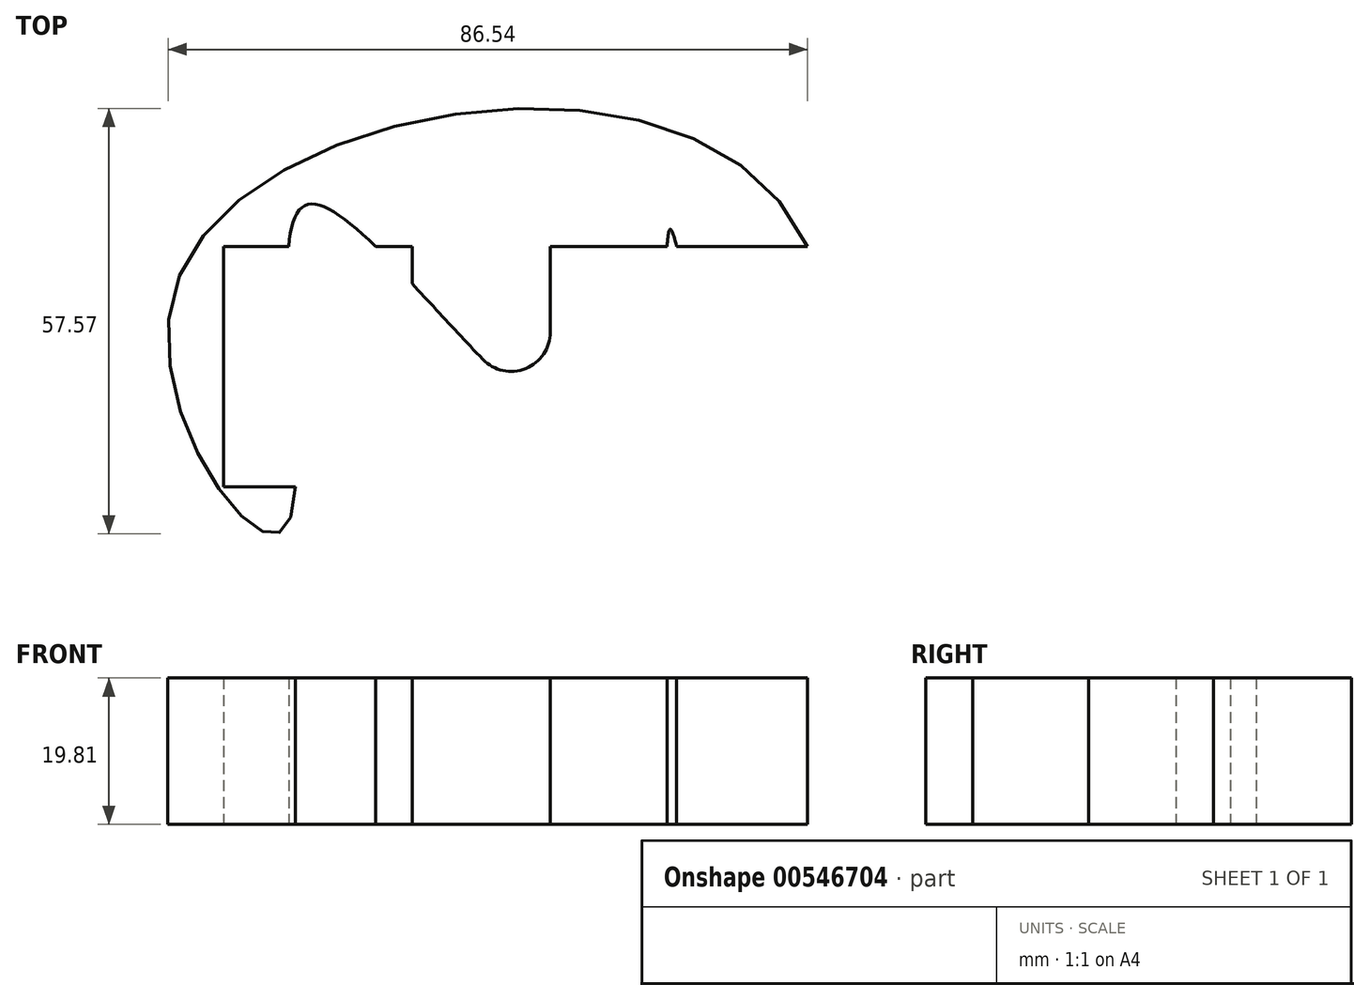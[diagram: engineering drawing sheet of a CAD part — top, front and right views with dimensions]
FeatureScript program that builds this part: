
annotation { "Feature Type Name" : "Feature", "Feature Type Description" : "" }
export const myFeature = defineFeature(function(context is Context, id is Id, definition is map)
    precondition{}
    {
        {
            var Q0;
            Q0=qCreatedBy(makeId("Top.planeOp"),FACE);
            var sketch = newSketch(context, id + "F0", { "sketchPlane" : qUnion([Q0])});
            skLineSegment(sketch, "E0.bottom", {"start": v(10.7, -17.95) * mm, "end": v(55.3, -17.95) * mm});
            skLineSegment(sketch, "E0.top", {"start": v(10.7, -50.52) * mm, "end": v(55.3, -50.52) * mm});
            skLineSegment(sketch, "E0.left", {"start": v(10.7, -17.95) * mm, "end": v(10.7, -50.52) * mm});
            skLineSegment(sketch, "E0.right", {"start": v(55.3, -17.95) * mm, "end": v(55.3, -50.52) * mm});
            skLineSegment(sketch, "E1.bottom", {"start": v(-8, -17.95) * mm, "end": v(-33.5, -17.95) * mm});
            skLineSegment(sketch, "E1.top", {"start": v(-8, -50.52) * mm, "end": v(-33.5, -50.52) * mm});
            skLineSegment(sketch, "E1.left", {"start": v(-8, -17.95) * mm, "end": v(-8, -50.52) * mm});
            skLineSegment(sketch, "E1.right", {"start": v(-33.5, -17.95) * mm, "end": v(-33.5, -50.52) * mm});
            skFitSpline(sketch, "E2", {"points": [v(-39.95, -23.23) * mm, v(-25.37, -56.28) * mm, v(-22.3, -12.33) * mm, v(19.82, -45.42) * mm, v(26.93, -15.64) * mm, v(41.1, -63.65) * mm, v(41.57, -11.71) * mm, v(-39.95, -23.23) * mm]});
            skSolve(sketch);
        }
        {
            var Q0;
            {var subQ9=sQuery(id+"F0.wireOp",EDGE,"E0.left");Q0=makeQuery(id+"F0.imprint","IMPRINT",FACE,{"disambiguationData":[TD([[makeQuery(id+"F0.imprint","IMPRINT",EDGE,{"derivedFrom":subQ9}),-1.0]])]});}
            extrude(context, id + "F1", {"entities" : qUnion([Q0]), "depth" : 19.8 * mm, "offsetDistance" : 25.4 * mm});
        }
        {
            var Q0;
            Q0=makeQuery(id+"F1.opExtrude","SWEPT_EDGE",EDGE,{"disambiguationData":[OSD([sQuery(id+"F0.wireOp",EDGE,"E0.left"),sQuery(id+"F0.wireOp",EDGE,"E2")])]});
            fillet(context, id + "F2", {"entities" : qUnion([Q0]), "radius" : 5.3 * mm, "tangentPropagation" : true, "allowEdgeOverflow" : false});
        }
    });
